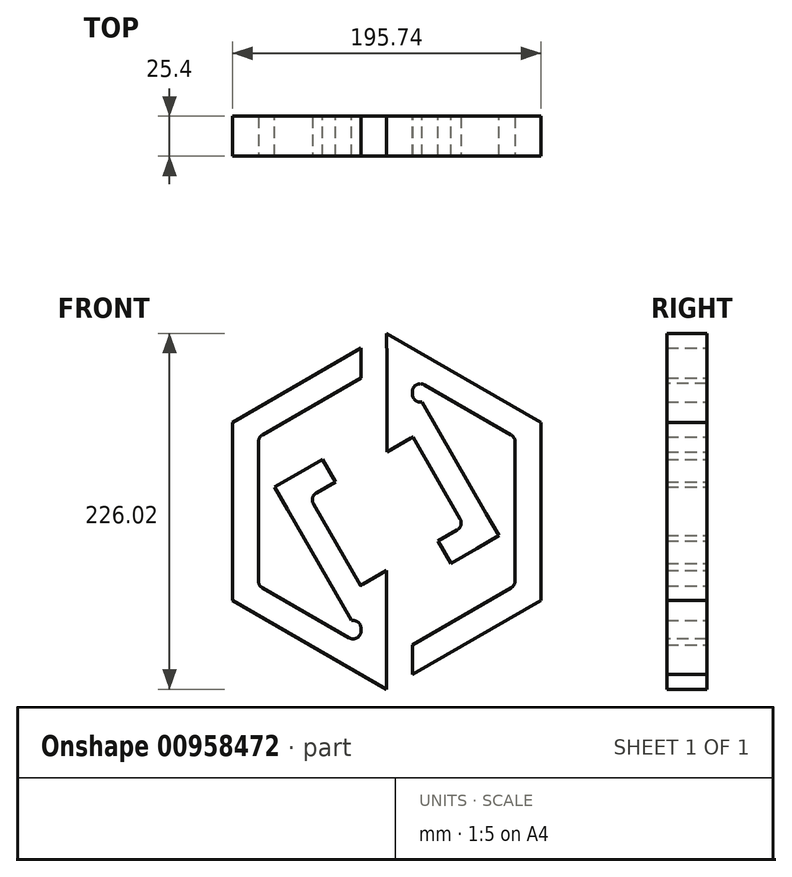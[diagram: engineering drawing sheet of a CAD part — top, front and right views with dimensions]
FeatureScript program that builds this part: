
annotation { "Feature Type Name" : "Feature", "Feature Type Description" : "" }
export const myFeature = defineFeature(function(context is Context, id is Id, definition is map)
    precondition{}
    {
        {
            var Q0;
            Q0=qCreatedBy(makeId("Front.planeOp"),FACE);
            var sketch = newSketch(context, id + "F0", { "sketchPlane" : qUnion([Q0])});
            skLineSegment(sketch, "E0", {"start": v(-97.87, 56.55) * mm, "end": v(-97.83, -56.48) * mm});
            skLineSegment(sketch, "E1", {"start": v(-97.83, -56.48) * mm, "end": v(0, -113.01) * mm});
            skLineSegment(sketch, "E2", {"start": v(0, -113.01) * mm, "end": v(-0.02, -94.16) * mm});
            skLineSegment(sketch, "E3", {"start": v(-0.02, -94.16) * mm, "end": v(-0.04, -37.61) * mm});
            skLineSegment(sketch, "E4", {"start": v(-0.04, -37.61) * mm, "end": v(-16.45, -47.09) * mm});
            skLineSegment(sketch, "E5", {"start": v(-16.45, -47.09) * mm, "end": v(-16.48, -47.33) * mm});
            skLineSegment(sketch, "E6", {"start": v(-16.48, -47.33) * mm, "end": v(-16.54, -47.24) * mm});
            skLineSegment(sketch, "E7", {"start": v(-16.54, -47.24) * mm, "end": v(-49.13, 9.22) * mm});
            skLineSegment(sketch, "E8", {"start": v(-49.13, 9.22) * mm, "end": v(-32.6, 18.77) * mm});
            skLineSegment(sketch, "E9", {"start": v(-32.6, 18.77) * mm, "end": v(-40.8, 32.97) * mm});
            skLineSegment(sketch, "E10", {"start": v(-40.8, 32.97) * mm, "end": v(-57.26, 23.47) * mm});
            skLineSegment(sketch, "E11", {"start": v(-57.26, 23.47) * mm, "end": v(-71.32, 15.35) * mm});
            skLineSegment(sketch, "E12", {"start": v(-71.32, 15.35) * mm, "end": v(-63.16, 1.22) * mm});
            skLineSegment(sketch, "E13", {"start": v(-63.16, 1.22) * mm, "end": v(-22.37, -69.44) * mm});
            skLineSegment(sketch, "E14", {"start": v(-22.37, -69.44) * mm, "end": v(-16.32, -65.95) * mm});
            skLineSegment(sketch, "E15", {"start": v(-16.32, -65.95) * mm, "end": v(-16.32, -84.75) * mm});
            skLineSegment(sketch, "E16", {"start": v(-16.32, -84.75) * mm, "end": v(-81.5, -47.1) * mm});
            skLineSegment(sketch, "E17", {"start": v(-81.5, -47.1) * mm, "end": v(-81.52, 47.05) * mm});
            skLineSegment(sketch, "E18", {"start": v(-81.52, 47.05) * mm, "end": v(-16.28, 84.72) * mm});
            skLineSegment(sketch, "E19", {"start": v(-16.28, 84.72) * mm, "end": v(-16.32, 103.63) * mm});
            skLineSegment(sketch, "E20", {"start": v(-16.32, 103.63) * mm, "end": v(-97.87, 56.55) * mm});
            skLineSegment(sketch, "E21", {"start": v(97.87, -56.55) * mm, "end": v(97.84, 56.48) * mm});
            skLineSegment(sketch, "E22", {"start": v(97.84, 56.48) * mm, "end": v(0, 113.01) * mm});
            skLineSegment(sketch, "E23", {"start": v(0, 113.01) * mm, "end": v(0.02, 94.16) * mm});
            skLineSegment(sketch, "E24", {"start": v(0.02, 94.16) * mm, "end": v(0.04, 37.62) * mm});
            skLineSegment(sketch, "E25", {"start": v(0.04, 37.62) * mm, "end": v(16.45, 47.09) * mm});
            skLineSegment(sketch, "E26", {"start": v(16.45, 47.09) * mm, "end": v(16.48, 47.33) * mm});
            skLineSegment(sketch, "E27", {"start": v(16.48, 47.33) * mm, "end": v(16.54, 47.23) * mm});
            skLineSegment(sketch, "E28", {"start": v(16.54, 47.23) * mm, "end": v(49.13, -9.22) * mm});
            skLineSegment(sketch, "E29", {"start": v(49.13, -9.22) * mm, "end": v(32.6, -18.77) * mm});
            skLineSegment(sketch, "E30", {"start": v(32.6, -18.77) * mm, "end": v(40.8, -32.97) * mm});
            skLineSegment(sketch, "E31", {"start": v(40.8, -32.97) * mm, "end": v(57.26, -23.47) * mm});
            skLineSegment(sketch, "E32", {"start": v(57.26, -23.47) * mm, "end": v(71.32, -15.35) * mm});
            skLineSegment(sketch, "E33", {"start": v(71.32, -15.35) * mm, "end": v(63.16, -1.22) * mm});
            skLineSegment(sketch, "E34", {"start": v(63.16, -1.22) * mm, "end": v(22.37, 69.44) * mm});
            skLineSegment(sketch, "E35", {"start": v(22.37, 69.44) * mm, "end": v(16.32, 65.95) * mm});
            skLineSegment(sketch, "E36", {"start": v(16.32, 65.95) * mm, "end": v(16.32, 84.75) * mm});
            skLineSegment(sketch, "E37", {"start": v(16.32, 84.75) * mm, "end": v(81.5, 47.1) * mm});
            skLineSegment(sketch, "E38", {"start": v(81.5, 47.1) * mm, "end": v(81.52, -47.05) * mm});
            skLineSegment(sketch, "E39", {"start": v(81.52, -47.05) * mm, "end": v(16.28, -84.72) * mm});
            skLineSegment(sketch, "E40", {"start": v(16.28, -84.72) * mm, "end": v(16.32, -103.63) * mm});
            skLineSegment(sketch, "E41", {"start": v(16.32, -103.63) * mm, "end": v(97.87, -56.55) * mm});
            skSolve(sketch);
        }
        {
            var Q0;
            Q0 = qSketchRegion(id + "F0", true);
            extrude(context, id + "F1", {"entities" : qUnion([Q0]), "depth" : 25.4 * mm, "offsetDistance" : 25.4 * mm});
        }
        {
            var Q0;
            Q0=makeQuery(id+"F1.opExtrude","SWEPT_EDGE",EDGE,{"disambiguationData":[OSD([sQuery(id+"F0.wireOp",EDGE,"E16"),sQuery(id+"F0.wireOp",EDGE,"E17")])]});
            var Q1;
            Q1=makeQuery(id+"F1.opExtrude","SWEPT_EDGE",EDGE,{"disambiguationData":[OSD([sQuery(id+"F0.wireOp",EDGE,"E15"),sQuery(id+"F0.wireOp",EDGE,"E16")])]});
            var Q2;
            Q2=makeQuery(id+"F1.opExtrude","SWEPT_EDGE",EDGE,{"disambiguationData":[OSD([sQuery(id+"F0.wireOp",EDGE,"E14"),sQuery(id+"F0.wireOp",EDGE,"E15")])]});
            var Q3;
            Q3=makeQuery(id+"F1.opExtrude","SWEPT_EDGE",EDGE,{"disambiguationData":[OSD([sQuery(id+"F0.wireOp",EDGE,"E17"),sQuery(id+"F0.wireOp",EDGE,"E18")])]});
            var Q4;
            Q4=makeQuery(id+"F1.opExtrude","SWEPT_EDGE",EDGE,{"disambiguationData":[OSD([sQuery(id+"F0.wireOp",EDGE,"E7"),sQuery(id+"F0.wireOp",EDGE,"E8")])]});
            var Q5;
            Q5=makeQuery(id+"F1.opExtrude","SWEPT_EDGE",EDGE,{"disambiguationData":[OSD([sQuery(id+"F0.wireOp",EDGE,"E4"),sQuery(id+"F0.wireOp",EDGE,"E5")])]});
            var Q6;
            Q6=makeQuery(id+"F1.opExtrude","SWEPT_EDGE",EDGE,{"disambiguationData":[OSD([sQuery(id+"F0.wireOp",EDGE,"E28"),sQuery(id+"F0.wireOp",EDGE,"E29")])]});
            var Q7;
            Q7=makeQuery(id+"F1.opExtrude","SWEPT_EDGE",EDGE,{"disambiguationData":[OSD([sQuery(id+"F0.wireOp",EDGE,"E25"),sQuery(id+"F0.wireOp",EDGE,"E26")])]});
            var Q8;
            Q8=makeQuery(id+"F1.opExtrude","SWEPT_EDGE",EDGE,{"disambiguationData":[OSD([sQuery(id+"F0.wireOp",EDGE,"E36"),sQuery(id+"F0.wireOp",EDGE,"E37")])]});
            var Q9;
            Q9=makeQuery(id+"F1.opExtrude","SWEPT_EDGE",EDGE,{"disambiguationData":[OSD([sQuery(id+"F0.wireOp",EDGE,"E35"),sQuery(id+"F0.wireOp",EDGE,"E36")])]});
            var Q10;
            Q10=makeQuery(id+"F1.opExtrude","SWEPT_EDGE",EDGE,{"disambiguationData":[OSD([sQuery(id+"F0.wireOp",EDGE,"E37"),sQuery(id+"F0.wireOp",EDGE,"E38")])]});
            var Q11;
            Q11=makeQuery(id+"F1.opExtrude","SWEPT_EDGE",EDGE,{"disambiguationData":[OSD([sQuery(id+"F0.wireOp",EDGE,"E38"),sQuery(id+"F0.wireOp",EDGE,"E39")])]});
            fillet(context, id + "F2", {"entities" : qUnion([Q0, Q1, Q2, Q3, Q4, Q5, Q6, Q7, Q8, Q9, Q10, Q11]), "radius" : 5.08 * mm, "tangentPropagation" : true, "allowEdgeOverflow" : false});
        }
    });
